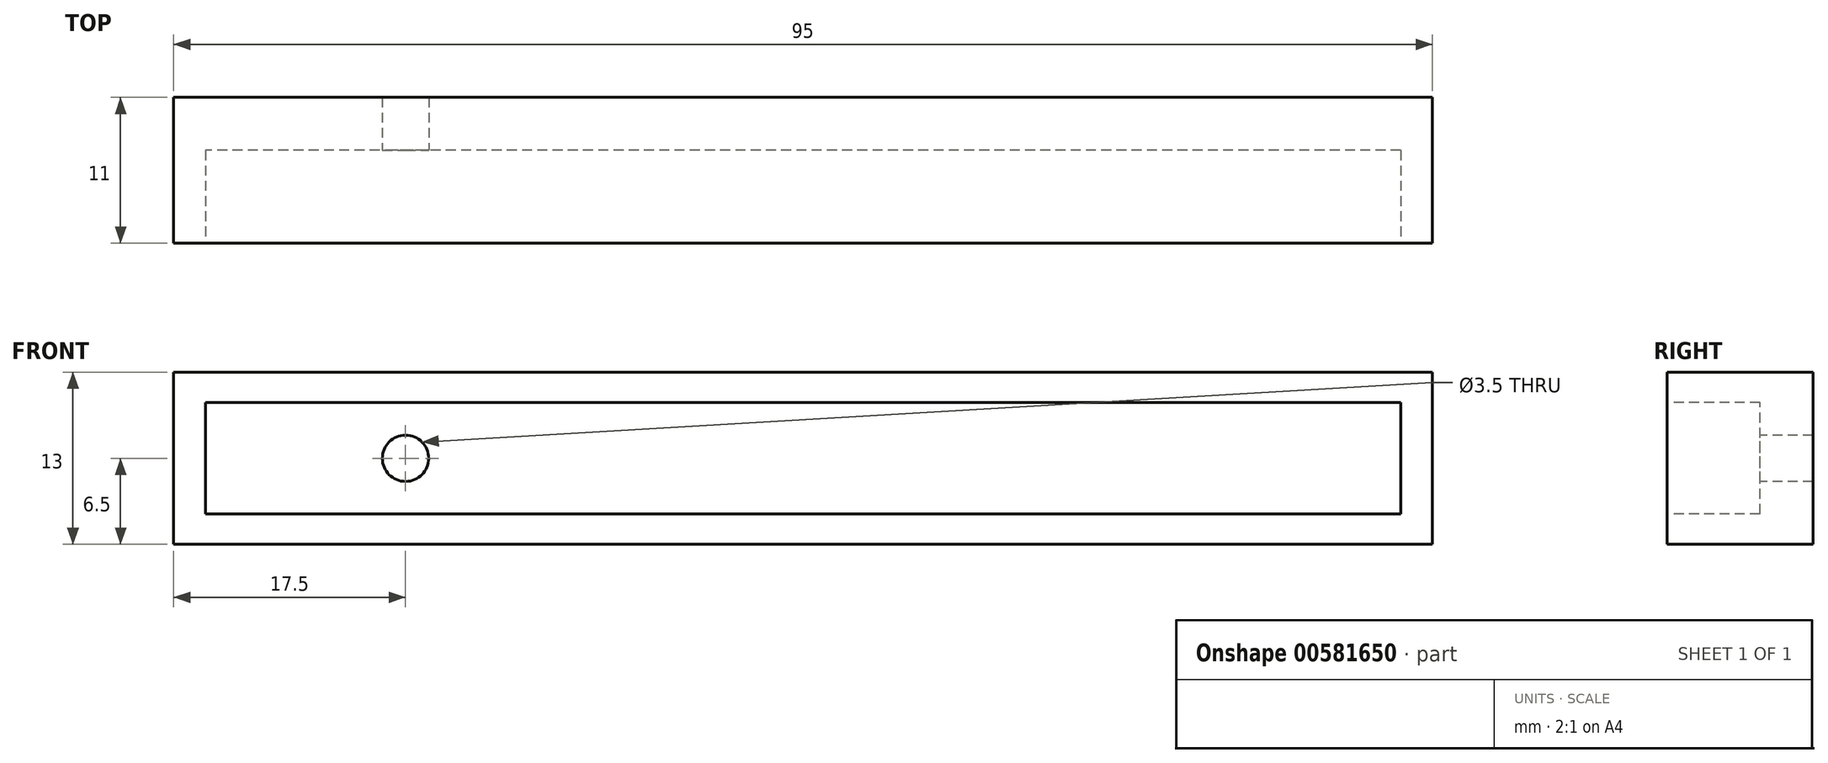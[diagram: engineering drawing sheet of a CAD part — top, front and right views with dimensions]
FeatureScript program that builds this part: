
annotation { "Feature Type Name" : "Feature", "Feature Type Description" : "" }
export const myFeature = defineFeature(function(context is Context, id is Id, definition is map)
    precondition{}
    {
        {
            var Q0;
            Q0=qCreatedBy(makeId("Front.planeOp"),FACE);
            var sketch = newSketch(context, id + "F0", { "sketchPlane" : qUnion([Q0])});
            skLineSegment(sketch, "E0.bottom", {"start": v(47.5, -6.5) * mm, "end": v(-47.5, -6.5) * mm});
            skLineSegment(sketch, "E0.top", {"start": v(47.5, 6.5) * mm, "end": v(-47.5, 6.5) * mm});
            skLineSegment(sketch, "E0.left", {"start": v(47.5, -6.5) * mm, "end": v(47.5, 6.5) * mm});
            skLineSegment(sketch, "E0.right", {"start": v(-47.5, -6.5) * mm, "end": v(-47.5, 6.5) * mm});
            skPoint(sketch, "E0.middle", {"position": v(0, 0) * mm});
            skSolve(sketch);
        }
        {
            var Q0;
            Q0=makeQuery(id+"F0.imprint","IMPRINT",FACE,{"disambiguationData":[TD([[makeQuery(id+"F0.imprint","IMPRINT",EDGE,{"derivedFrom":sQuery(id+"F0.wireOp",EDGE,"E0.bottom")}),-1.0]])]});
            extrude(context, id + "F1", {"entities" : qUnion([Q0]), "depth" : 11 * mm, "offsetDistance" : 25 * mm});
        }
        {
            var Q0;
            Q0=makeQuery(id+"F1.opExtrude","CAP_FACE",FACE,{"disambiguationData":[OSD([sQuery(id+"F0.wireOp",EDGE,"E0.bottom"),sQuery(id+"F0.wireOp",EDGE,"E0.top"),sQuery(id+"F0.wireOp",EDGE,"E0.left"),sQuery(id+"F0.wireOp",EDGE,"E0.right")])],"isStart":false});
            var sketch = newSketch(context, id + "F2", { "sketchPlane" : qUnion([Q0])});
            skLineSegment(sketch, "E1.bottom", {"start": v(45.1, -4.2) * mm, "end": v(-45.1, -4.2) * mm});
            skLineSegment(sketch, "E1.top", {"start": v(45.1, 4.2) * mm, "end": v(-45.1, 4.2) * mm});
            skLineSegment(sketch, "E1.left", {"start": v(45.1, -4.2) * mm, "end": v(45.1, 4.2) * mm});
            skLineSegment(sketch, "E1.right", {"start": v(-45.1, -4.2) * mm, "end": v(-45.1, 4.2) * mm});
            skPoint(sketch, "E1.middle", {"position": v(0, 0) * mm});
            skSolve(sketch);
        }
        {
            var Q0;
            Q0=makeQuery(id+"F2.imprint","IMPRINT",FACE,{"disambiguationData":[TD([[makeQuery(id+"F2.imprint","IMPRINT",EDGE,{"derivedFrom":sQuery(id+"F2.wireOp",EDGE,"E1.bottom")}),-1.0]])]});
            extrude(context, id + "F3", {"entities" : qUnion([Q0]), "operationType" : NewBodyOperationType.REMOVE, "oppositeDirection" : true, "depth" : 7 * mm, "offsetDistance" : 25 * mm});
        }
        {
            var Q0;
            Q0=makeQuery(id+"F3.boolean.opBoolean","COPY",FACE,{"derivedFrom":makeQuery(id+"F3.opExtrude","CAP_FACE",FACE,{"disambiguationData":[OSD([sQuery(id+"F2.wireOp",EDGE,"E1.bottom"),sQuery(id+"F2.wireOp",EDGE,"E1.top"),sQuery(id+"F2.wireOp",EDGE,"E1.left"),sQuery(id+"F2.wireOp",EDGE,"E1.right")])],"isStart":false})});
            var sketch = newSketch(context, id + "F4", { "sketchPlane" : qUnion([Q0])});
            skCircle(sketch, "E2", {"center": v(-30, 0) * mm, "radius": 1.75 * mm});
            skSolve(sketch);
        }
        {
            var Q0;
            Q0=makeQuery(id+"F4.imprint","IMPRINT",FACE,{"disambiguationData":[TD([[makeQuery(id+"F4.imprint","IMPRINT",EDGE,{"derivedFrom":sQuery(id+"F4.wireOp",EDGE,"E2")}),1.0]])]});
            extrude(context, id + "F5", {"entities" : qUnion([Q0]), "operationType" : NewBodyOperationType.REMOVE, "endBound" : BoundingType.UP_TO_NEXT, "oppositeDirection" : true, "depth" : 25 * mm, "offsetDistance" : 25 * mm});
        }
    });
